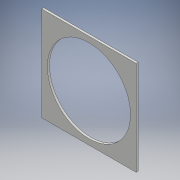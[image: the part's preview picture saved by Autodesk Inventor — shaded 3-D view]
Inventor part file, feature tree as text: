
AUTODESK INVENTOR PART (.ipt)
format: ipt  version: 2018 (Build 220112000, 112)  size: 222,720 bytes
history: native  units: mm
features: extrude x2, sketch x2
ambient origin geometry x8: Origin, YZ Plane, XZ Plane, XY Plane, X Axis, Y Axis, Z Axis, Center Point
bodies: Solid1 (feature_tree)
feature tree (4):
  extrude  "Extrusion1"  Depth=110.0mm
  extrude  "Extrusion2"  Depth=2.5mm TaperAngle=0.0deg
  sketch  "Sketch1"  dims[d0=110.0mm d1=110.0mm]
  sketch  "Sketch2"  dims[d2=2.5mm d3=0.0mm d5=2.5mm d6=0.0mm]
